# Revit family: Accessory-Robe_Hook-KOHLER-Stages-K-30377T_1
name_source: partatom
category: Specialty Equipment
units: mm (PartAtom-declared; Revit-internal decimal feet)

## family parameters
Cut with Voids When Loaded = No
Host = Face
OmniClass Number = 23.31.25.27
OmniClass Title = Robe Hooks
Part Type = Normal
Room Calculation Point = No
Round Connector Dimension = Use Diameter
Shared = No

## types (6) — shared parameters
ADA Compliant = No
Assembly Code = C1030200
Date Modified = 11/10/2022
Default Elevation = 42"
Description = Grid Jump Hook (Removable)
Height = 1 9/16"
Length = 13/16"
Manufacturer = Kohler Co.
Master Format 2014 = 10 28 00
Master Format 2014 Name = Toilet, Bath, and Laundry Accessories
Material = Premium Metal Construction
Product Documentation Link = https://files.kohler.com.cn
Product Name = Stages
URL = http://www.kohler.com.cn
WaterSense Certified = No
Width = 1"

## per-type parameters (varying)
| type | Finish | Model | Product Page URL | Type |
| 2MB-Vibrant Brushed Moderne Brass | Kohler-Metal-2MB-Vibrant_Brushed_Moderne_Brass | K-30377T-2MB |  | 1 |
| AF-Vibrant French Gold | Kohler-Metal-AF-Vibrant_French_Gold | K-30377T-AF | https://www.kohler.com.cn | 2 |
| BL-Matte Black | Kohler-Metal-BL-Matte_Black | K-30377T-BL | https://www.kohler.com.cn | 3 |
| BN-Vibrant Brushed Nickel | Kohler-Metal-BN-Vibrant_Brushed_Nickel | K-30377T-BN | https://www.kohler.com.cn | 4 |
| CP-Polished Chrome | Kohler-Metal-CP-Polished_Chrome | K-30377T-CP | https://www.kohler.com.cn | 5 |
| RGD-Polished Rose Gold | Kohler-Metal-RGD-Polished_Rose_Gold | K-30377T-RGD | https://www.kohler.com.cn | 6 |

## geometry (parser evidence)
native form markers: Sweep x5
no freeform markers — native parametric forms only
